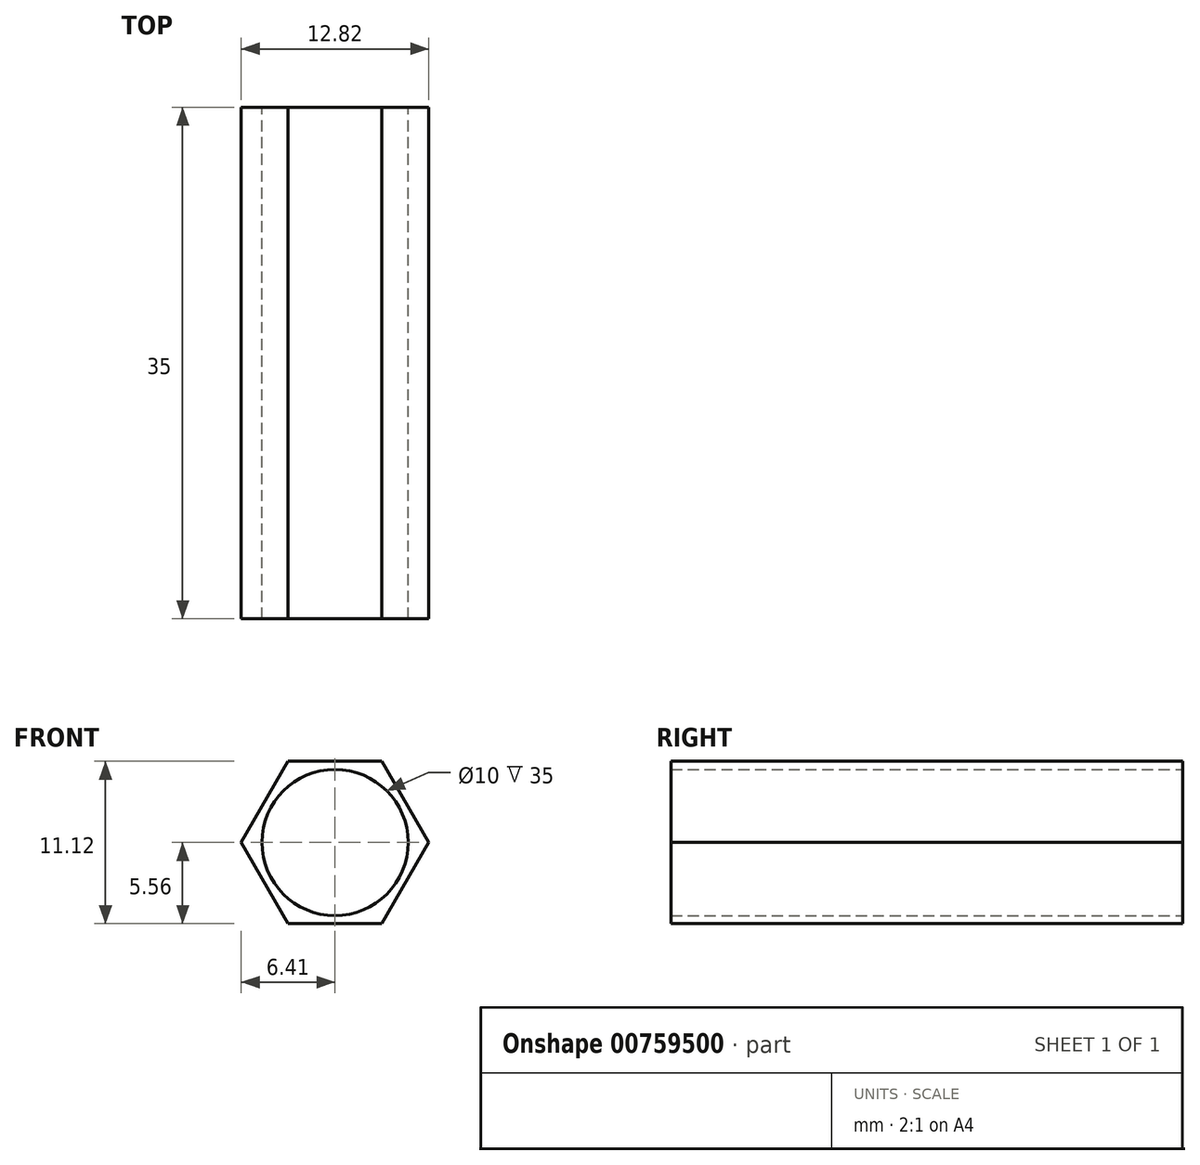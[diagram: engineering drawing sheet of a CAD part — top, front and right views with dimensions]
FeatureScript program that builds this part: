
annotation { "Feature Type Name" : "Feature", "Feature Type Description" : "" }
export const myFeature = defineFeature(function(context is Context, id is Id, definition is map)
    precondition{}
    {
        {
            var Q0;
            Q0=qCreatedBy(makeId("Front.planeOp"),FACE);
            var sketch = newSketch(context, id + "F0", { "sketchPlane" : qUnion([Q0])});
            skCircle(sketch, "E0.cCircle", {"center": v(0, 0) * mm, "radius": 5.56 * mm, "construction": true});
            skLineSegment(sketch, "E0.0", {"start": v(-3.2, 5.55) * mm, "end": v(3.2, 5.55) * mm});
            skLineSegment(sketch, "E0.1", {"start": v(3.2, 5.55) * mm, "end": v(6.41, 0) * mm});
            skLineSegment(sketch, "E0.2", {"start": v(6.41, 0) * mm, "end": v(3.2, -5.55) * mm});
            skLineSegment(sketch, "E0.3", {"start": v(3.2, -5.55) * mm, "end": v(-3.2, -5.56) * mm});
            skLineSegment(sketch, "E0.4", {"start": v(-3.2, -5.56) * mm, "end": v(-6.41, 0) * mm});
            skLineSegment(sketch, "E0.5", {"start": v(-6.41, 0) * mm, "end": v(-3.2, 5.55) * mm});
            skPoint(sketch, "E0.0.midPoint", {"position": v(0, 5.56) * mm});
            skSolve(sketch);
        }
        {
            var Q0;
            Q0 = qSketchRegion(id + "F0", true);
            extrude(context, id + "F1", {"entities" : qUnion([Q0]), "depth" : 35 * mm, "offsetDistance" : 25 * mm});
        }
        {
            var Q0;
            Q0=qCreatedBy(makeId("Front.planeOp"),FACE);
            var sketch = newSketch(context, id + "F2", { "sketchPlane" : qUnion([Q0])});
            skCircle(sketch, "E1", {"center": v(0, 0) * mm, "radius": 5 * mm});
            skSolve(sketch);
        }
        {
            var Q0;
            Q0 = qSketchRegion(id + "F2", true);
            extrude(context, id + "F3", {"entities" : qUnion([Q0]), "operationType" : NewBodyOperationType.REMOVE, "depth" : 52.2 * mm, "offsetDistance" : 25 * mm});
        }
    });
